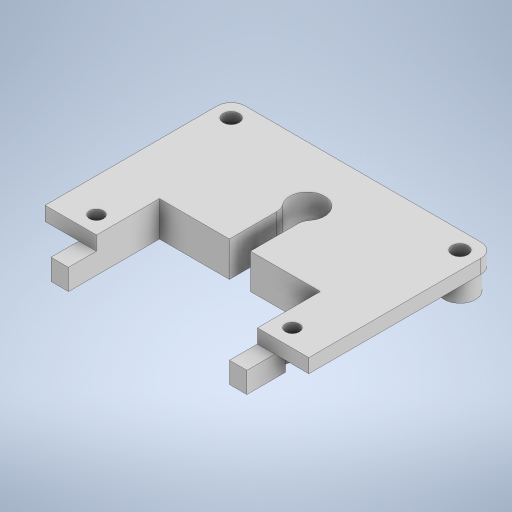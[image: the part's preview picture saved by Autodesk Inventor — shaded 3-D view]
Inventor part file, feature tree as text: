
AUTODESK INVENTOR PART (.ipt)
format: ipt  version: 2024.2 (Build 282272000, 272)  size: 405,504 bytes
history: native  units: mm
features: extrude x13, sketch x13, fillet x3, projected_geometry x2
ambient origin geometry x8: Origin, YZ Plane, XZ Plane, XY Plane, X Axis, Y Axis, Z Axis, Center Point
bodies: Solid1 (feature_tree)
feature tree (31):
  extrude  "Extrusion1"  Depth=38.5mm
  extrude  "Extrusion2"  Depth=4.0mm
  extrude  "Extrusion3"  Depth=4.0mm
  extrude  "Extrusion4"  Depth=3.0mm TaperAngle=0.0deg
  fillet  "Fillet1"  Radius=48.2mm
  extrude  "Extrusion6"  Depth=4.85mm
  extrude  "Extrusion9"  Depth=2.0mm TaperAngle=0.0deg
  extrude  "Extrusion10"  Depth=2.35mm
  fillet  "Fillet2"  Radius=2.35mm
  extrude  "Extrusion11"  Depth=2.35mm
  extrude  "Extrusion12"  Depth=4.5mm
  extrude  "Extrusion13"  Depth=4.5mm
  extrude  "Extrusion14"  Depth=2.35mm
  fillet  "Fillet3"  Radius=2.35mm
  extrude  "Extrusion15"  Depth=2.0mm
  extrude  "Extrusion17"  Depth=2.0mm
  sketch  "Sketch1"  dims[d0=28.0mm d1=38.5mm]
  sketch  "Sketch2"  dims[d6=3.0mm d7=0.0mm d8=4.0mm]
  sketch  "Sketch3"  dims[d9=4.0mm d10=4.0mm]
  sketch  "Sketch4"  dims[d11=4.0mm d12=3.0mm d13=0.0mm d14=48.2mm]
  sketch  "Sketch5"  dims[d15=37.7mm d16=4.85mm]
  sketch  "Sketch8"  dims[d17=4.85mm d18=2.0mm d19=0.0mm]
  sketch  "Sketch9"  dims[d20=4.5mm d21=2.35mm d22=2.35mm]
  sketch  "Sketch10"  dims[d23=4.5mm d24=2.35mm]
  sketch  "Sketch11"  dims[d25=2.35mm d26=4.5mm]
  sketch  "Sketch12"  dims[d27=2.35mm d28=4.5mm]
  sketch  "Sketch13"  dims[d29=2.35mm d30=2.35mm d31=2.35mm]
  sketch  "Sketch14"  dims[d32=3.0mm d33=0.0mm d34=2.0mm]
  projected_geometry  "Projected Loop1"
  projected_geometry  "Projected Loop2"
  sketch  "Sketch16"  dims[d45=2.0mm d46=2.0mm d51=0.0mm d52=0.0mm d68=3.5mm d69=3.125mm d70=18.85mm d71=0.0mm d72=0.0mm d73=28.0mm d76=2.0mm d77=1.0mm d78=0.0mm d79=0.0mm d80=2.0mm d81=24.1mm d82=4.85mm d83=23.0mm d84=13.0mm d85=7.35mm d86=6.5mm d87=0.0mm d88=0.0mm d90=0.0mm d91=0.0mm d92=5.0mm d93=3.125mm d94=18.85mm d95=0.0mm d96=0.0mm d97=3.0mm d98=0.0mm d99=0.0mm d100=2.0mm d101=2.3mm d102=2.3mm d103=0.0mm d104=0.0mm d109=4.0mm d110=4.0mm d111=2.0mm d112=0.0mm d63=0.5mm d64=0.872665mm d65=0.5mm d66=0.872665mm]
